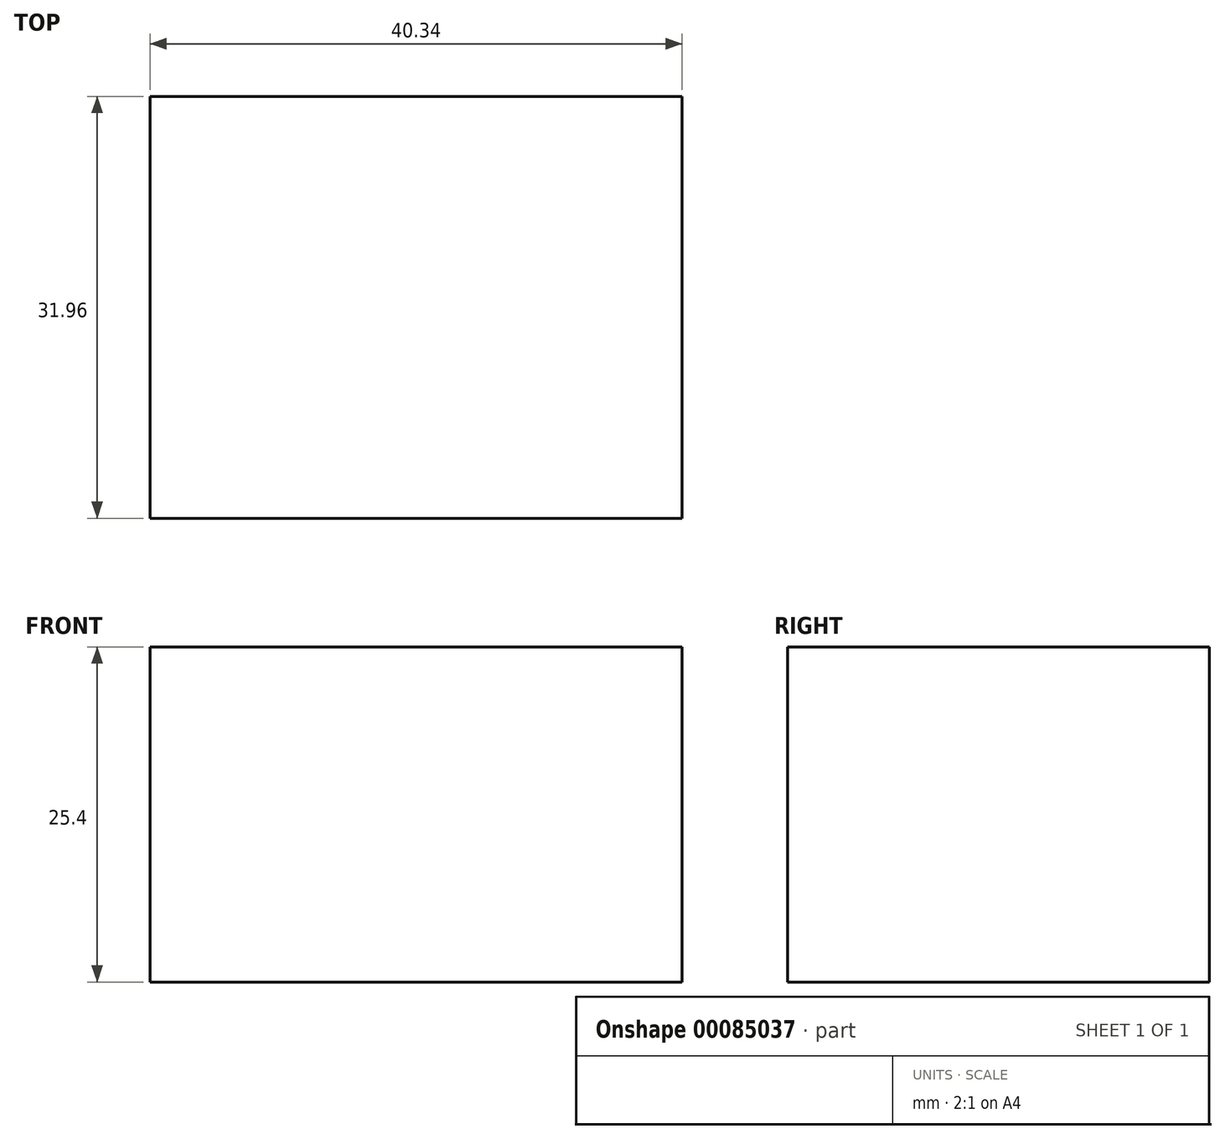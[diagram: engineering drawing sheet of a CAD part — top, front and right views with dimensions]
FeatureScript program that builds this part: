
annotation { "Feature Type Name" : "Feature", "Feature Type Description" : "" }
export const myFeature = defineFeature(function(context is Context, id is Id, definition is map)
    precondition{}
    {
        {
            var Q0;
            Q0=qCreatedBy(makeId("Top.planeOp"),FACE);
            var sketch = newSketch(context, id + "F0", { "sketchPlane" : qUnion([Q0])});
            skLineSegment(sketch, "E0.bottom", {"start": v(0, 0) * mm, "end": v(40.34, 0) * mm});
            skLineSegment(sketch, "E0.top", {"start": v(0, -31.96) * mm, "end": v(40.34, -31.96) * mm});
            skLineSegment(sketch, "E0.left", {"start": v(0, 0) * mm, "end": v(0, -31.96) * mm});
            skLineSegment(sketch, "E0.right", {"start": v(40.34, 0) * mm, "end": v(40.34, -31.96) * mm});
            skSolve(sketch);
        }
        {
            var Q0;
            Q0=makeQuery(id+"F0.imprint","IMPRINT",FACE,{"disambiguationData":[TD([[makeQuery(id+"F0.imprint","IMPRINT",EDGE,{"derivedFrom":sQuery(id+"F0.wireOp",EDGE,"E0.bottom")}),-1.0]])]});
            extrude(context, id + "F1", {"entities" : qUnion([Q0]), "depth" : 25.4 * mm});
        }
    });
